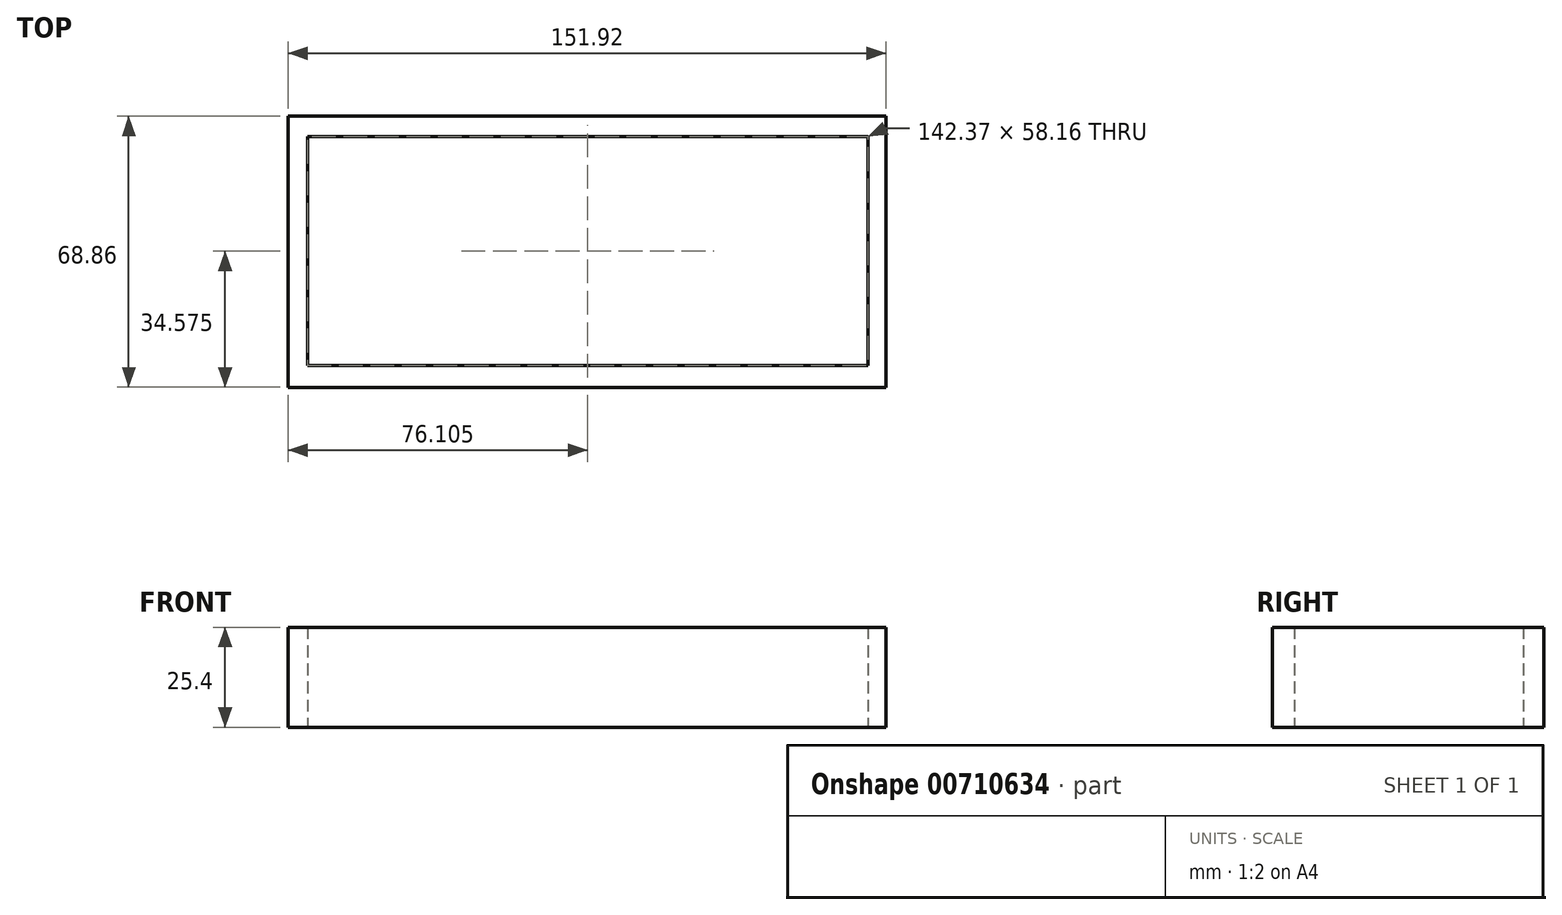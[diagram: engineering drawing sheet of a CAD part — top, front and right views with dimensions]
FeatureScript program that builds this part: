
annotation { "Feature Type Name" : "Feature", "Feature Type Description" : "" }
export const myFeature = defineFeature(function(context is Context, id is Id, definition is map)
    precondition{}
    {
        {
            var Q0;
            Q0=qCreatedBy(makeId("Top.planeOp"),FACE);
            var sketch = newSketch(context, id + "F0", { "sketchPlane" : qUnion([Q0])});
            skLineSegment(sketch, "E0.bottom", {"start": v(-75.96, 34.43) * mm, "end": v(75.96, 34.43) * mm});
            skLineSegment(sketch, "E0.top", {"start": v(-75.96, -34.43) * mm, "end": v(75.96, -34.43) * mm});
            skLineSegment(sketch, "E0.left", {"start": v(-75.96, 34.43) * mm, "end": v(-75.96, -34.43) * mm});
            skLineSegment(sketch, "E0.right", {"start": v(75.96, 34.43) * mm, "end": v(75.96, -34.43) * mm});
            skPoint(sketch, "E0.middle", {"position": v(0, 0) * mm});
            skPoint(sketch, "E1.orphan", {"position": v(3.04, 0) * mm});
            skLineSegment(sketch, "E2.bottom", {"start": v(-71.04, 29.23) * mm, "end": v(71.33, 29.23) * mm});
            skLineSegment(sketch, "E2.top", {"start": v(-71.04, -28.94) * mm, "end": v(71.33, -28.94) * mm});
            skLineSegment(sketch, "E2.left", {"start": v(-71.04, 29.23) * mm, "end": v(-71.04, -28.94) * mm});
            skLineSegment(sketch, "E2.right", {"start": v(71.33, 29.23) * mm, "end": v(71.33, -28.94) * mm});
            skSolve(sketch);
        }
        {
            var Q0;
            Q0=makeQuery(id+"F0.imprint","IMPRINT",FACE,{"disambiguationData":[TD([[makeQuery(id+"F0.imprint","IMPRINT",EDGE,{"derivedFrom":sQuery(id+"F0.wireOp",EDGE,"E0.bottom")}),-1.0]])]});
            extrude(context, id + "F1", {"entities" : qUnion([Q0]), "depth" : 25.4 * mm, "offsetDistance" : 25.4 * mm});
        }
    });
